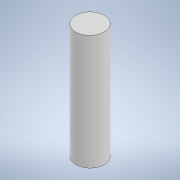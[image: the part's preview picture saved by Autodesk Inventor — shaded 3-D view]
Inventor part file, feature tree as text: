
AUTODESK INVENTOR PART (.ipt)
format: ipt  version: 2020 (Build 240168000, 168)  size: 89,600 bytes
history: native  units: mm
features: extrude x1, sketch x1
ambient origin geometry x8: Origin, YZ Plane, XZ Plane, XY Plane, X Axis, Y Axis, Z Axis, Center Point
bodies: Solid1 (feature_tree)
feature tree (2):
  extrude  "Extrusion1"  Depth=12.0mm TaperAngle=0.0deg
  sketch  "Sketch1"  dims[d0=3.0mm d1=12.0mm d2=0.0mm]
